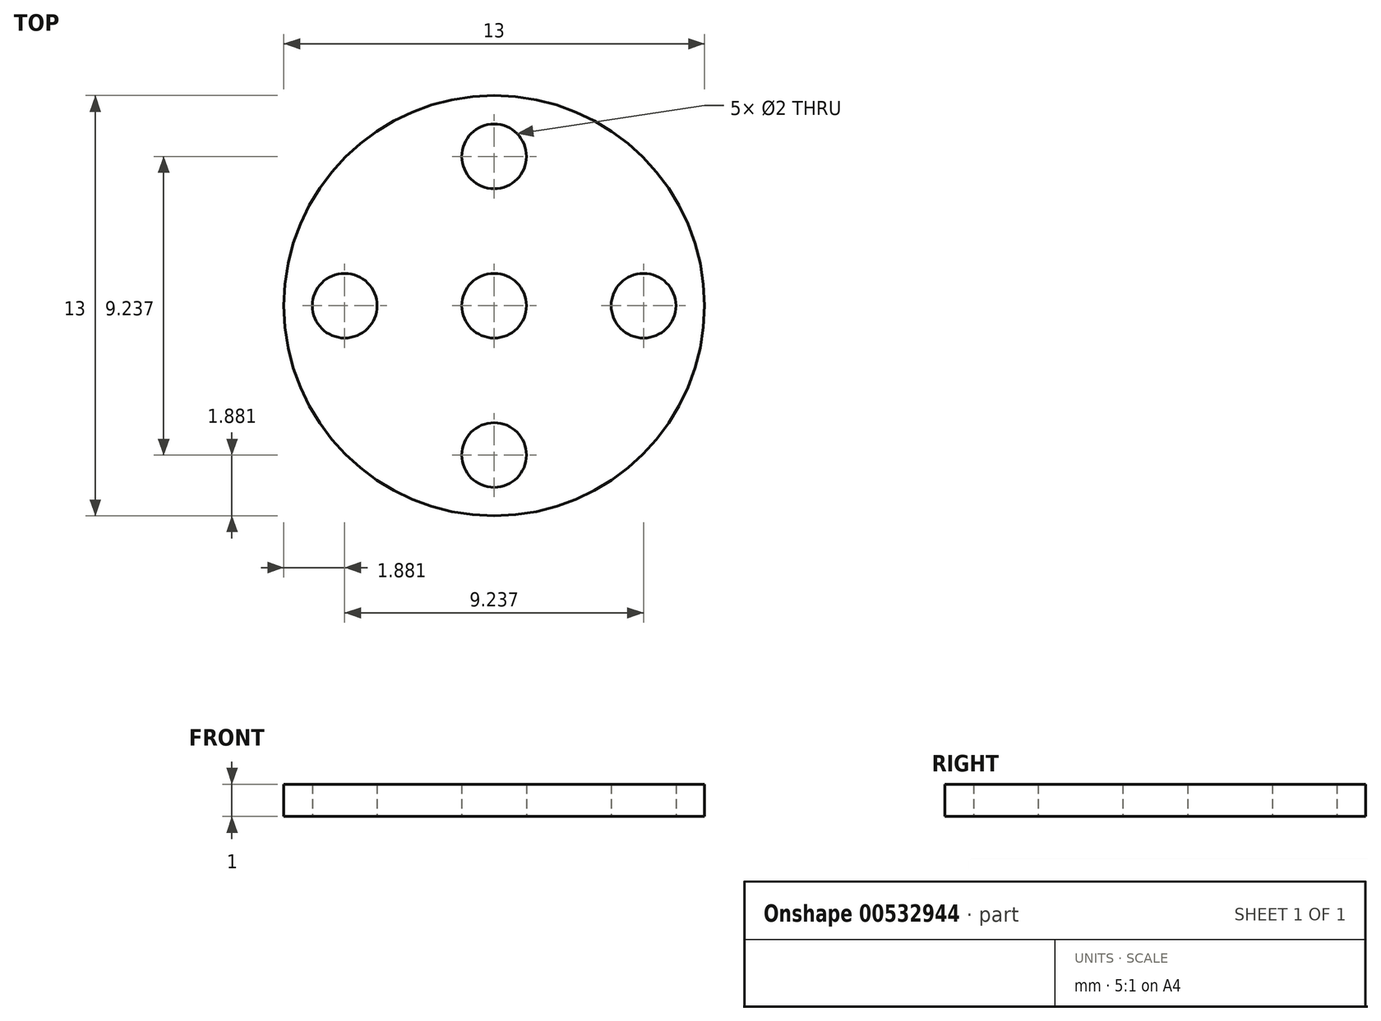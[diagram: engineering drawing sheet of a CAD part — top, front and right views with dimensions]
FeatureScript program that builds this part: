
annotation { "Feature Type Name" : "Feature", "Feature Type Description" : "" }
export const myFeature = defineFeature(function(context is Context, id is Id, definition is map)
    precondition{}
    {
        {
            var Q0;
            Q0=qCreatedBy(makeId("Top.planeOp"),FACE);
            var sketch = newSketch(context, id + "F0", { "sketchPlane" : qUnion([Q0])});
            skCircle(sketch, "E0", {"center": v(0, 0) * mm, "radius": 6.5 * mm});
            skCircle(sketch, "E1", {"center": v(0, 0) * mm, "radius": 1 * mm});
            skCircle(sketch, "E2", {"center": v(0, 4.62) * mm, "radius": 1 * mm});
            skCircle(sketch, "E3.1.0", {"center": v(-4.62, 0) * mm, "radius": 1 * mm});
            skCircle(sketch, "E3.2.0", {"center": v(0, -4.62) * mm, "radius": 1 * mm});
            skCircle(sketch, "E3.3.0", {"center": v(4.62, 0) * mm, "radius": 1 * mm});
            skSolve(sketch);
        }
        {
            var Q0;
            Q0 = qSketchRegion(id + "F0", true);
            extrude(context, id + "F1", {"entities" : qUnion([Q0]), "depth" : 1 * mm, "offsetDistance" : 25 * mm});
        }
    });
